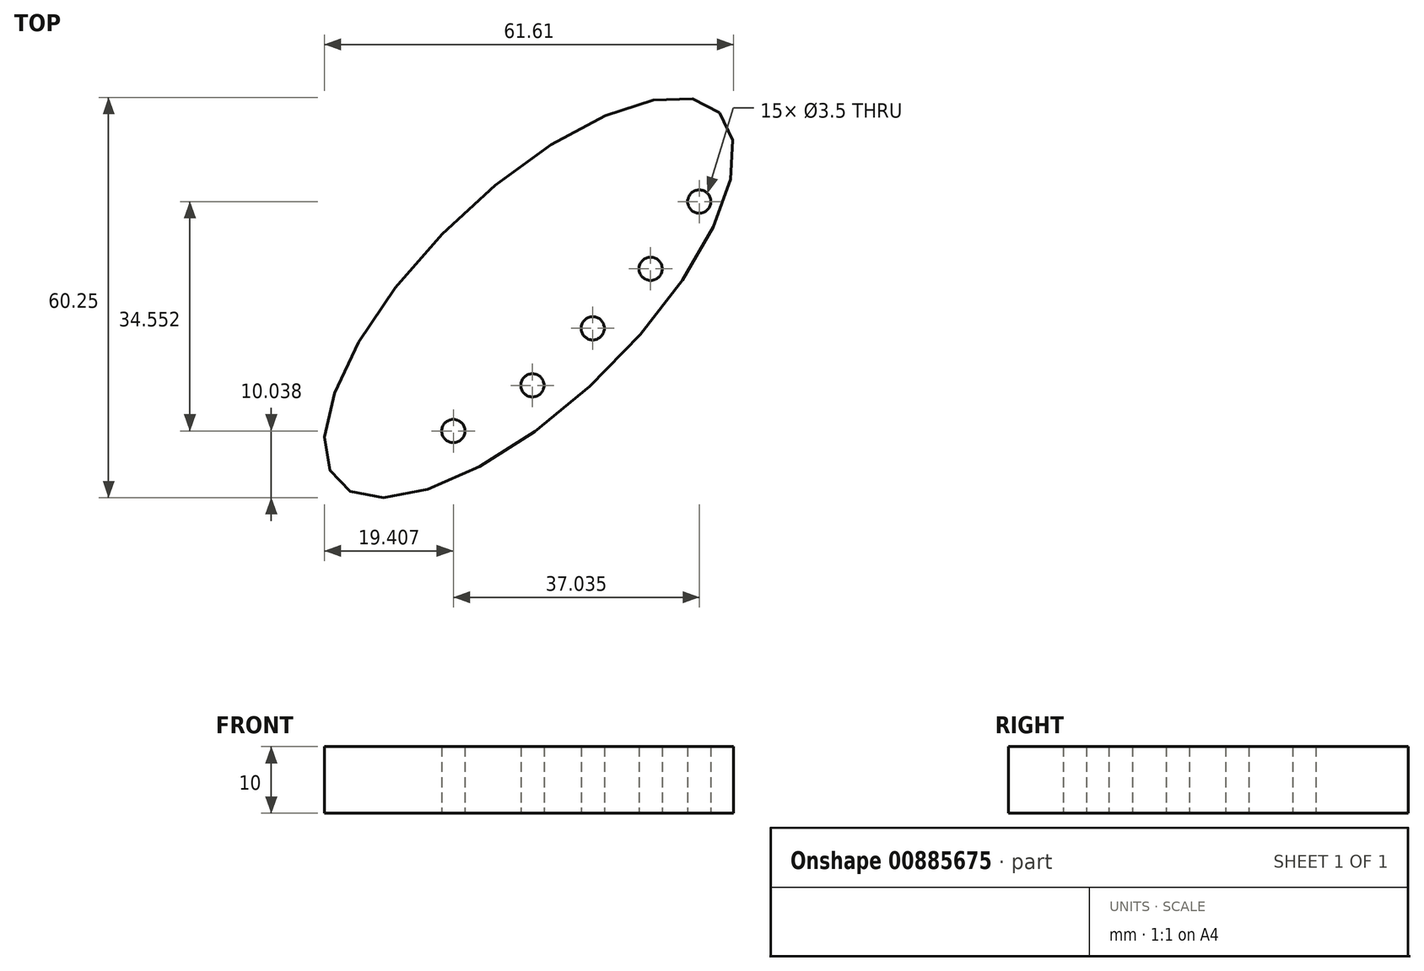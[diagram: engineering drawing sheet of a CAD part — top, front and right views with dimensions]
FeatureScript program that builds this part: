
annotation { "Feature Type Name" : "Feature", "Feature Type Description" : "" }
export const myFeature = defineFeature(function(context is Context, id is Id, definition is map)
    precondition{}
    {
        {
            var Q0;
            Q0=qCreatedBy(makeId("Top.planeOp"),FACE);
            var sketch = newSketch(context, id + "F0", { "sketchPlane" : qUnion([Q0])});
            skEllipse(sketch, "E0", {"center": v(-32.38, -16.39) * mm, "majorRadius": 40 * mm, "minorRadius": 16 * mm, "majorAxis": v(0.72, 0.7)});
            skCircle(sketch, "E1", {"center": v(-43.78, -36.47) * mm, "radius": 1.75 * mm});
            skCircle(sketch, "E2", {"center": v(-31.88, -29.6) * mm, "radius": 1.75 * mm});
            skCircle(sketch, "E3", {"center": v(-22.8, -21) * mm, "radius": 1.75 * mm});
            skCircle(sketch, "E4", {"center": v(-14.08, -12.04) * mm, "radius": 1.75 * mm});
            skCircle(sketch, "E5", {"center": v(-6.75, -1.92) * mm, "radius": 1.75 * mm});
            skSolve(sketch);
        }
        {
            var Q0;
            Q0 = qSketchRegion(id + "F0", true);
            extrude(context, id + "F1", {"entities" : qUnion([Q0]), "depth" : 10 * mm, "offsetDistance" : 25 * mm});
        }
    });
